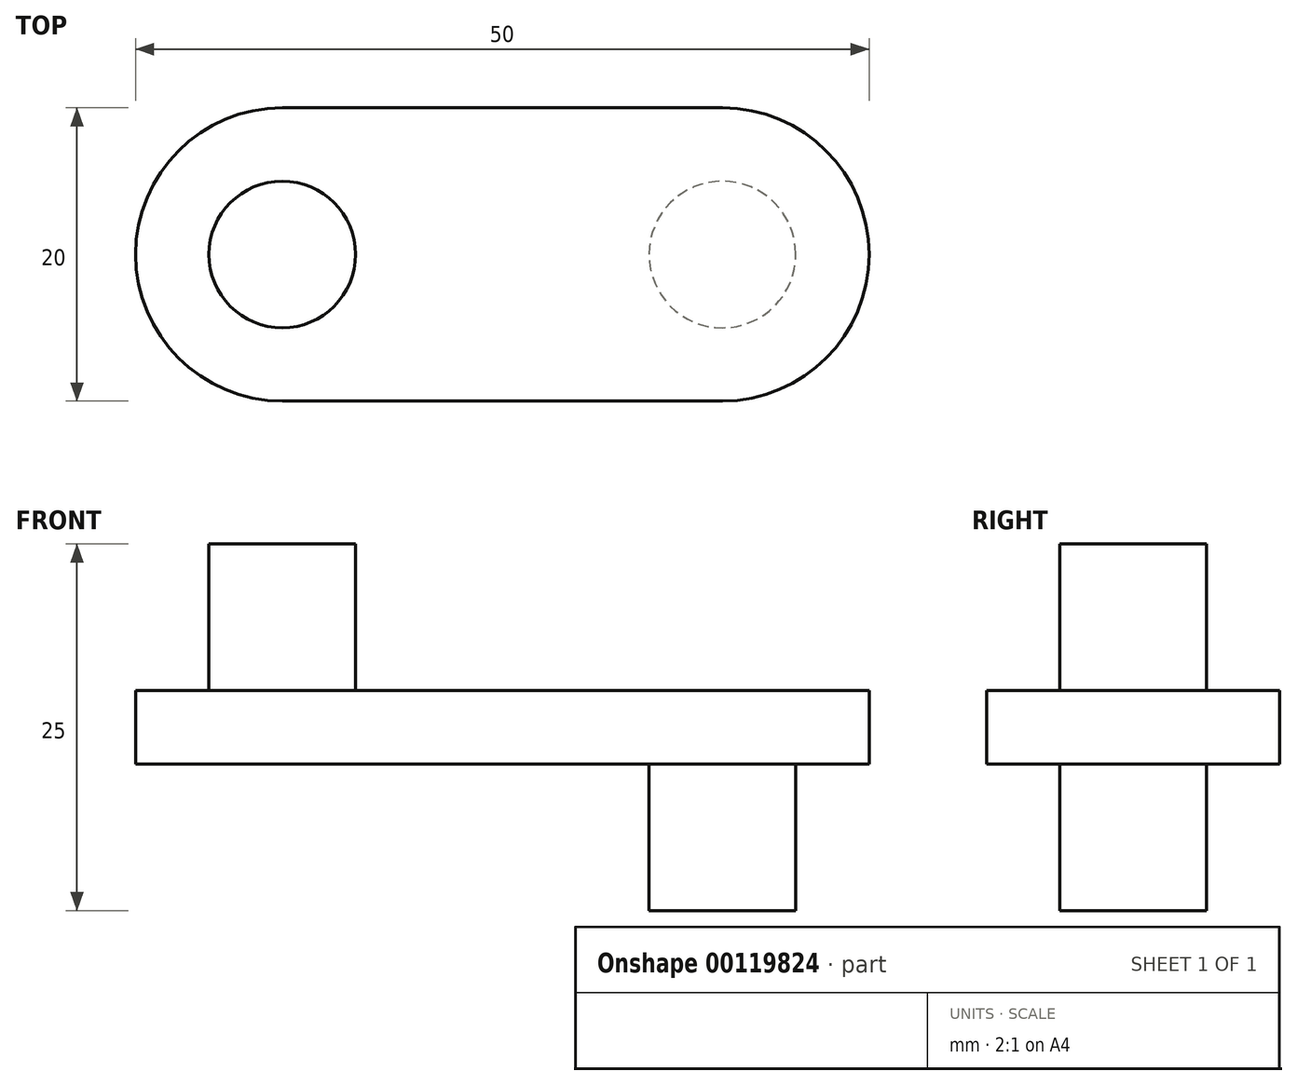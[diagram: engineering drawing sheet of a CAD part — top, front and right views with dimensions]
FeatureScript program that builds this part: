
annotation { "Feature Type Name" : "Feature", "Feature Type Description" : "" }
export const myFeature = defineFeature(function(context is Context, id is Id, definition is map)
    precondition{}
    {
        {
            var Q0;
            Q0=qCreatedBy(makeId("Top.planeOp"),FACE);
            var sketch = newSketch(context, id + "F0", { "sketchPlane" : qUnion([Q0])});
            skArc(sketch, "E0", {"start": v(-15, 10) * mm, "mid": v(-25, 0) * mm, "end": v(-15, -10) * mm});
            skArc(sketch, "E1", {"start": v(15, -10) * mm, "mid": v(25, 0) * mm, "end": v(15, 10) * mm});
            skLineSegment(sketch, "E2", {"start": v(-15, 10) * mm, "end": v(15, 10) * mm});
            skLineSegment(sketch, "E3", {"start": v(-15, -10) * mm, "end": v(15, -10) * mm});
            skSolve(sketch);
        }
        {
            var Q0;
            Q0=qSketchRegion(id+"F0",true);
            extrude(context, id + "F1", {"entities" : qUnion([Q0]), "depth" : 5 * mm});
        }
        {
            var Q0;
            Q0=makeQuery(id+"F1.opExtrude","CAP_FACE",FACE,{"disambiguationData":[OSD([sQuery(id+"F0.wireOp",EDGE,"E0"),sQuery(id+"F0.wireOp",EDGE,"E1"),sQuery(id+"F0.wireOp",EDGE,"E2"),sQuery(id+"F0.wireOp",EDGE,"E3")])],"isStart":false});
            var sketch = newSketch(context, id + "F2", { "sketchPlane" : qUnion([Q0])});
            skCircle(sketch, "E4", {"center": v(-15, 0) * mm, "radius": 5 * mm});
            skSolve(sketch);
        }
        {
            var Q0;
            Q0=qSketchRegion(id+"F2",true);
            extrude(context, id + "F3", {"entities" : qUnion([Q0]), "operationType" : NewBodyOperationType.ADD, "depth" : 10 * mm});
        }
        {
            var Q0;
            Q0=makeQuery(id+"F1.opExtrude","CAP_FACE",FACE,{"disambiguationData":[OSD([sQuery(id+"F0.wireOp",EDGE,"E0"),sQuery(id+"F0.wireOp",EDGE,"E1"),sQuery(id+"F0.wireOp",EDGE,"E2"),sQuery(id+"F0.wireOp",EDGE,"E3")])],"isStart":true});
            var sketch = newSketch(context, id + "F4", { "sketchPlane" : qUnion([Q0])});
            skCircle(sketch, "E5", {"center": v(15, 0) * mm, "radius": 5 * mm});
            skSolve(sketch);
        }
        {
            var Q0;
            Q0=qSketchRegion(id+"F4",true);
            extrude(context, id + "F5", {"entities" : qUnion([Q0]), "operationType" : NewBodyOperationType.ADD, "depth" : 10 * mm});
        }
    });
